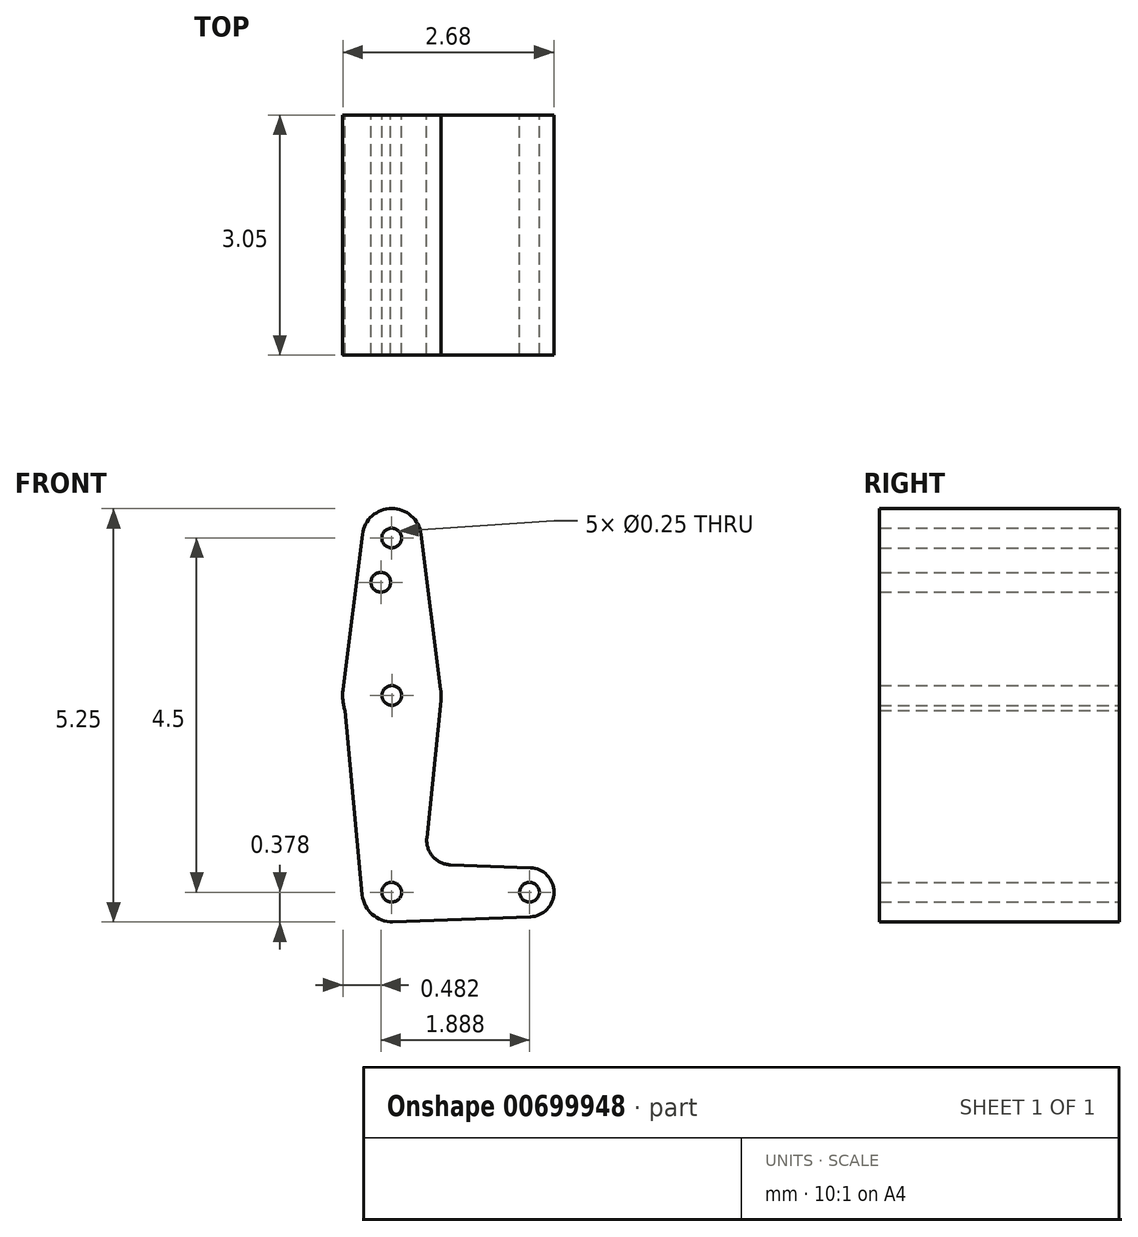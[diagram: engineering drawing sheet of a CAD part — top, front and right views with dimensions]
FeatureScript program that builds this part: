
annotation { "Feature Type Name" : "Feature", "Feature Type Description" : "" }
export const myFeature = defineFeature(function(context is Context, id is Id, definition is map)
    precondition{}
    {
        {
            var Q0;
            Q0=qCreatedBy(makeId("Front.planeOp"),FACE);
            var sketch = newSketch(context, id + "F0", { "sketchPlane" : qUnion([Q0])});
            skLineSegment(sketch, "E0", {"start": v(0, 2.53) * mm, "end": v(0, -1.97) * mm});
            skLineSegment(sketch, "E1", {"start": v(0, -1.97) * mm, "end": v(1.75, -1.97) * mm});
            skCircle(sketch, "E2", {"center": v(0, 2.53) * mm, "radius": 0.38 * mm});
            skCircle(sketch, "E3", {"center": v(0, 0.53) * mm, "radius": 0.62 * mm});
            skCircle(sketch, "E4", {"center": v(0, -1.97) * mm, "radius": 0.38 * mm});
            skCircle(sketch, "E5", {"center": v(1.75, -1.97) * mm, "radius": 0.31 * mm});
            skLineSegment(sketch, "E6", {"start": v(0.37, 2.57) * mm, "end": v(0.63, 0.53) * mm});
            skLineSegment(sketch, "E7", {"start": v(0.63, 0.53) * mm, "end": v(0.45, -1.28) * mm});
            skLineSegment(sketch, "E8", {"start": v(-0.37, 2.57) * mm, "end": v(-0.62, 0.6) * mm});
            skLineSegment(sketch, "E9", {"start": v(-0.62, 0.6) * mm, "end": v(-0.37, -2) * mm});
            skLineSegment(sketch, "E10", {"start": v(1.76, -1.66) * mm, "end": v(0.75, -1.62) * mm});
            skLineSegment(sketch, "E11", {"start": v(1.76, -2.28) * mm, "end": v(0, -2.35) * mm});
            skCircle(sketch, "E12", {"center": v(0, 2.53) * mm, "radius": 0.12 * mm});
            skCircle(sketch, "E13", {"center": v(0, 0.53) * mm, "radius": 0.12 * mm});
            skCircle(sketch, "E14", {"center": v(-0.14, 1.97) * mm, "radius": 0.12 * mm});
            skCircle(sketch, "E15", {"center": v(0, -1.97) * mm, "radius": 0.12 * mm});
            skCircle(sketch, "E16", {"center": v(1.75, -1.97) * mm, "radius": 0.12 * mm});
            skArc(sketch, "E17.filletArc", {"start": v(0.45, -1.28) * mm, "mid": v(0.52, -1.52) * mm, "end": v(0.75, -1.62) * mm});
            skSolve(sketch);
        }
        {
            var Q0;
            Q0 = qSketchRegion(id + "F0", true);
            var Q1;
            {var subQ0=sQuery(id+"F0.wireOp",EDGE,"E4");var subQ1=sQuery(id+"F0.wireOp",EDGE,"E0");var subQ2=makeQuery(id+"F0.imprint","INTERSECT",VERTEX,{"derivedFrom":[subQ1,subQ0]});Q1=makeQuery(id+"F0.imprint","IMPRINT",FACE,{"disambiguationData":[TD([[makeQuery(id+"F0.imprint","IMPRINT",EDGE,{"disambiguationData":[TD([[subQ2,-1.0]])],"derivedFrom":subQ1}),1.0]])]});}
            extrude(context, id + "F1", {"entities" : qUnion([Q0, Q1]), "depth" : 3.05 * mm, "offsetDistance" : 25 * mm});
        }
    });
